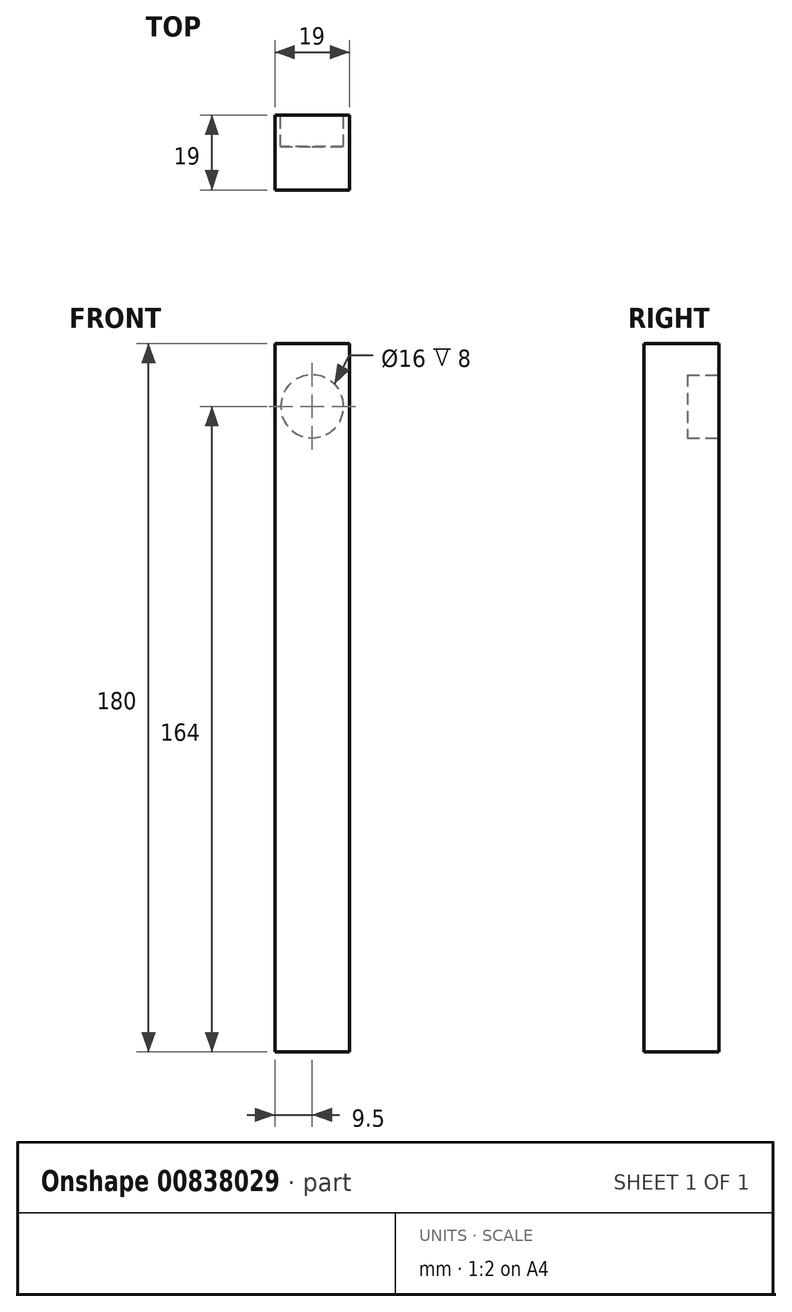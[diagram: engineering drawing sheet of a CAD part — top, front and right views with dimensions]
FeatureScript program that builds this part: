
annotation { "Feature Type Name" : "Feature", "Feature Type Description" : "" }
export const myFeature = defineFeature(function(context is Context, id is Id, definition is map)
    precondition{}
    {
        {
            var Q0;
            Q0=qCreatedBy(makeId("Top.planeOp"),FACE);
            var sketch = newSketch(context, id + "F0", { "sketchPlane" : qUnion([Q0])});
            skLineSegment(sketch, "E0.bottom", {"start": v(9.5, -9.5) * mm, "end": v(-9.5, -9.5) * mm});
            skLineSegment(sketch, "E0.top", {"start": v(9.5, 9.5) * mm, "end": v(-9.5, 9.5) * mm});
            skLineSegment(sketch, "E0.left", {"start": v(9.5, -9.5) * mm, "end": v(9.5, 9.5) * mm});
            skLineSegment(sketch, "E0.right", {"start": v(-9.5, -9.5) * mm, "end": v(-9.5, 9.5) * mm});
            skPoint(sketch, "E0.middle", {"position": v(0, 0) * mm});
            skSolve(sketch);
        }
        {
            var Q0;
            Q0 = qSketchRegion(id + "F0", true);
            extrude(context, id + "F1", {"entities" : qUnion([Q0]), "depth" : 180 * mm, "offsetDistance" : 25 * mm});
        }
        {
            var Q0;
            Q0=makeQuery(id+"F1.opExtrude","SWEPT_FACE",FACE,{"disambiguationData":[OSD([sQuery(id+"F0.wireOp",EDGE,"E0.top")])]});
            var sketch = newSketch(context, id + "F2", { "sketchPlane" : qUnion([Q0])});
            skPoint(sketch, "E1", {"position": v(0, 164) * mm});
            skCircle(sketch, "E2", {"center": v(0, 164) * mm, "radius": 8 * mm});
            skSolve(sketch);
        }
        {
            var Q0;
            Q0 = qSketchRegion(id + "F2", true);
            extrude(context, id + "F3", {"entities" : qUnion([Q0]), "operationType" : NewBodyOperationType.REMOVE, "oppositeDirection" : true, "depth" : 8 * mm, "offsetDistance" : 25 * mm});
        }
    });
